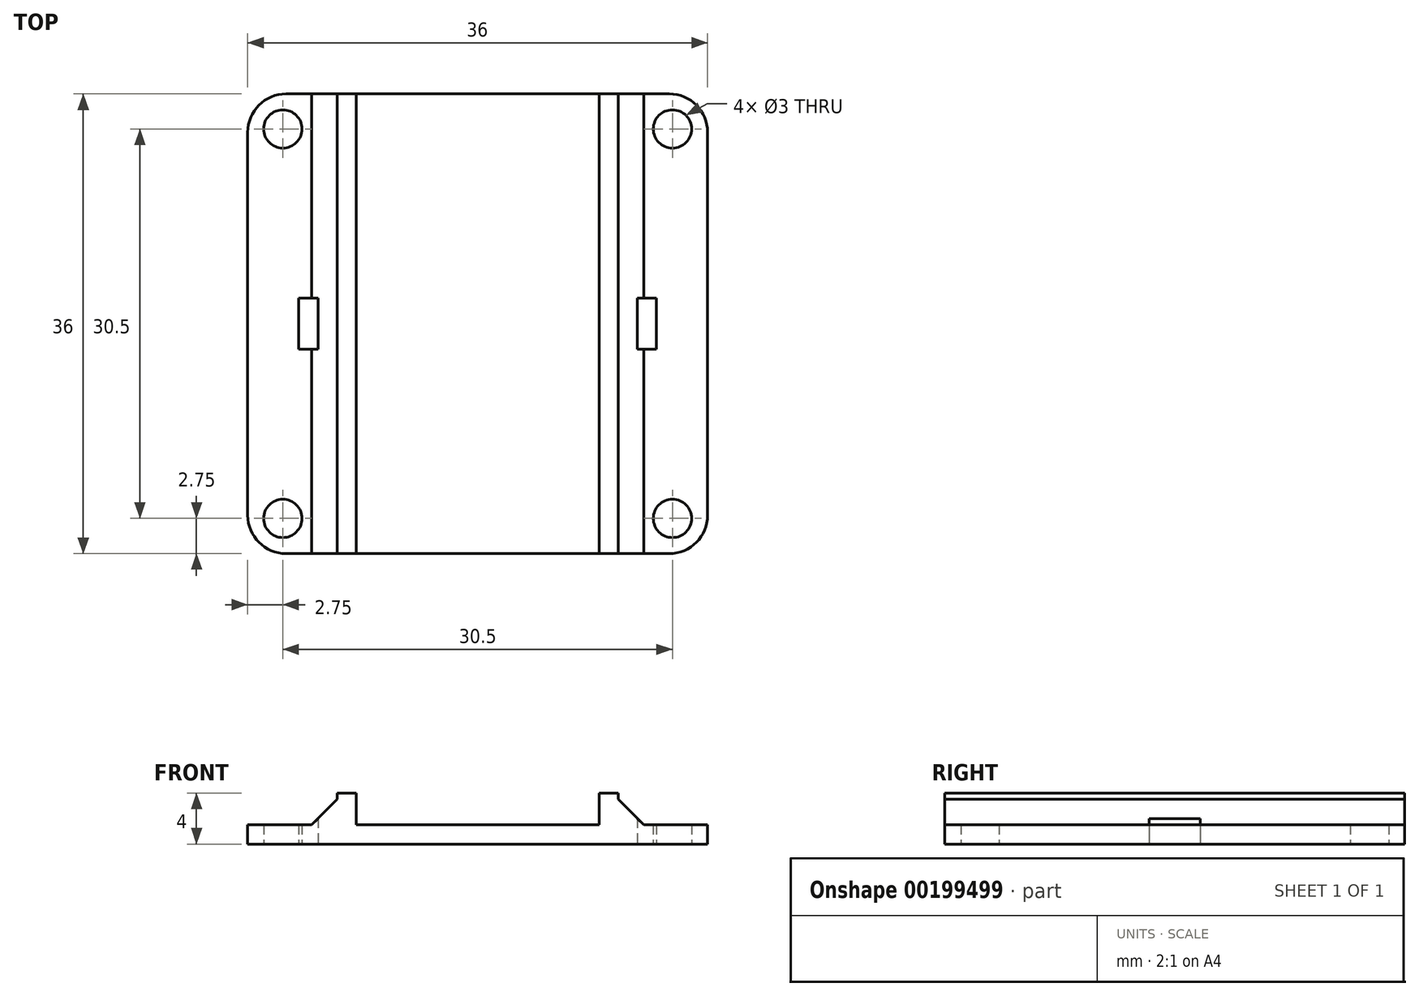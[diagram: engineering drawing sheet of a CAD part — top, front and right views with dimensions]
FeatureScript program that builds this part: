
annotation { "Feature Type Name" : "Feature", "Feature Type Description" : "" }
export const myFeature = defineFeature(function(context is Context, id is Id, definition is map)
    precondition{}
    {
        {
            var Q0;
            Q0=qCreatedBy(makeId("Top.planeOp"),FACE);
            var sketch = newSketch(context, id + "F0", { "sketchPlane" : qUnion([Q0])});
            skLineSegment(sketch, "E0.bottom", {"start": v(18, 18) * mm, "end": v(-18, 18) * mm});
            skLineSegment(sketch, "E0.top", {"start": v(18, -18) * mm, "end": v(-18, -18) * mm});
            skLineSegment(sketch, "E0.left", {"start": v(18, 18) * mm, "end": v(18, -18) * mm});
            skLineSegment(sketch, "E0.right", {"start": v(-18, 18) * mm, "end": v(-18, -18) * mm});
            skPoint(sketch, "E0.middle", {"position": v(0, 0) * mm});
            skLineSegment(sketch, "E1.bottom", {"start": v(15.25, 15.25) * mm, "end": v(-15.25, 15.25) * mm, "construction": true});
            skLineSegment(sketch, "E1.top", {"start": v(15.25, -15.25) * mm, "end": v(-15.25, -15.25) * mm, "construction": true});
            skLineSegment(sketch, "E1.left", {"start": v(15.25, 15.25) * mm, "end": v(15.25, -15.25) * mm, "construction": true});
            skLineSegment(sketch, "E1.right", {"start": v(-15.25, 15.25) * mm, "end": v(-15.25, -15.25) * mm, "construction": true});
            skCircle(sketch, "E2", {"center": v(-15.25, 15.25) * mm, "radius": 1.5 * mm});
            skCircle(sketch, "E3", {"center": v(15.25, 15.25) * mm, "radius": 1.5 * mm});
            skCircle(sketch, "E4", {"center": v(15.25, -15.25) * mm, "radius": 1.5 * mm});
            skCircle(sketch, "E5", {"center": v(-15.25, -15.25) * mm, "radius": 1.5 * mm});
            skLineSegment(sketch, "E6.bottom", {"start": v(-9.5, 18) * mm, "end": v(9.5, 18) * mm});
            skLineSegment(sketch, "E6.top", {"start": v(-9.5, -18) * mm, "end": v(9.5, -18) * mm});
            skLineSegment(sketch, "E6.left", {"start": v(-9.5, 18) * mm, "end": v(-9.5, -18) * mm});
            skLineSegment(sketch, "E6.right", {"start": v(9.5, 18) * mm, "end": v(9.5, -18) * mm});
            skLineSegment(sketch, "E7.bottom", {"start": v(-11, 18) * mm, "end": v(11, 18) * mm});
            skLineSegment(sketch, "E7.top", {"start": v(-11, -18) * mm, "end": v(11, -18) * mm});
            skLineSegment(sketch, "E7.left", {"start": v(-11, 18) * mm, "end": v(-11, -18) * mm});
            skLineSegment(sketch, "E7.right", {"start": v(11, 18) * mm, "end": v(11, -18) * mm});
            skPoint(sketch, "E8.centerSnap0", {"position": v(-15.25, 0) * mm});
            skPoint(sketch, "E9.centerSnap0", {"position": v(15.25, 0) * mm});
            skLineSegment(sketch, "E10", {"start": v(-11, 0) * mm, "end": v(-9.5, 0) * mm, "construction": true});
            skLineSegment(sketch, "E11", {"start": v(9.5, 0) * mm, "end": v(11, 0) * mm, "construction": true});
            skLineSegment(sketch, "E12.bottom", {"start": v(11, 2) * mm, "end": v(9.5, 2) * mm});
            skLineSegment(sketch, "E12.top", {"start": v(11, -2) * mm, "end": v(9.5, -2) * mm});
            skLineSegment(sketch, "E12.left", {"start": v(11, 2) * mm, "end": v(11, -2) * mm});
            skLineSegment(sketch, "E12.right", {"start": v(9.5, 2) * mm, "end": v(9.5, -2) * mm});
            skPoint(sketch, "E12.middle", {"position": v(10.25, 0) * mm});
            skLineSegment(sketch, "E13.bottom", {"start": v(-9.5, 2) * mm, "end": v(-11, 2) * mm});
            skLineSegment(sketch, "E13.top", {"start": v(-9.5, -2) * mm, "end": v(-11, -2) * mm});
            skLineSegment(sketch, "E13.left", {"start": v(-9.5, 2) * mm, "end": v(-9.5, -2) * mm});
            skLineSegment(sketch, "E13.right", {"start": v(-11, 2) * mm, "end": v(-11, -2) * mm});
            skPoint(sketch, "E13.middle", {"position": v(-10.25, 0) * mm});
            skLineSegment(sketch, "E14", {"start": v(-11, 2) * mm, "end": v(-12.5, 2) * mm, "construction": true});
            skLineSegment(sketch, "E15", {"start": v(-11, -2) * mm, "end": v(-12.5, -2) * mm, "construction": true});
            skLineSegment(sketch, "E16.bottom", {"start": v(-12.5, -2) * mm, "end": v(-14, -2) * mm});
            skLineSegment(sketch, "E16.top", {"start": v(-12.5, 2) * mm, "end": v(-14, 2) * mm});
            skLineSegment(sketch, "E16.left", {"start": v(-12.5, -2) * mm, "end": v(-12.5, 2) * mm});
            skLineSegment(sketch, "E16.right", {"start": v(-14, -2) * mm, "end": v(-14, 2) * mm});
            skLineSegment(sketch, "E17", {"start": v(0, -18) * mm, "end": v(0, 18) * mm, "construction": true});
            skLineSegment(sketch, "E18.MirrorCS", {"start": v(12.5, -2) * mm, "end": v(14, -2) * mm});
            skLineSegment(sketch, "E19.MirrorCS", {"start": v(14, -2) * mm, "end": v(14, 2) * mm});
            skLineSegment(sketch, "E20.MirrorCS", {"start": v(12.5, 2) * mm, "end": v(14, 2) * mm});
            skLineSegment(sketch, "E21.MirrorCS", {"start": v(12.5, -2) * mm, "end": v(12.5, 2) * mm});
            skSolve(sketch);
        }
        {
            var Q0;
            {var subQ0=sQuery(id+"F0.wireOp",EDGE,"E0.right");Q0=makeQuery(id+"F0.imprint","IMPRINT",FACE,{"disambiguationData":[TD([[makeQuery(id+"F0.imprint","IMPRINT",EDGE,{"derivedFrom":subQ0}),1.0]])]});}
            var Q1;
            {var subQ0=sQuery(id+"F0.wireOp",EDGE,"E6.left");Q1=makeQuery(id+"F0.imprint","IMPRINT",FACE,{"disambiguationData":[TD([[makeQuery(id+"F0.imprint","IMPRINT",EDGE,{"derivedFrom":subQ0}),-1.0]])]});}
            var Q2;
            {var subQ0=sQuery(id+"F0.wireOp",EDGE,"E6.right");Q2=makeQuery(id+"F0.imprint","IMPRINT",FACE,{"disambiguationData":[TD([[makeQuery(id+"F0.imprint","IMPRINT",EDGE,{"derivedFrom":subQ0}),1.0]])]});}
            var Q3;
            {var subQ0=sQuery(id+"F0.wireOp",EDGE,"E0.left");Q3=makeQuery(id+"F0.imprint","IMPRINT",FACE,{"disambiguationData":[TD([[makeQuery(id+"F0.imprint","IMPRINT",EDGE,{"derivedFrom":subQ0}),-1.0]])]});}
            var Q4;
            {var subQ0=sQuery(id+"F0.wireOp",EDGE,"E6.left");Q4=makeQuery(id+"F0.imprint","IMPRINT",FACE,{"disambiguationData":[TD([[makeQuery(id+"F0.imprint","IMPRINT",EDGE,{"derivedFrom":subQ0}),1.0]])]});}
            var Q5;
            Q5=makeQuery(id+"F0.imprint","IMPRINT",FACE,{"disambiguationData":[TD([[makeQuery(id+"F0.imprint","IMPRINT",EDGE,{"derivedFrom":sQuery(id+"F0.wireOp",EDGE,"E13.bottom")}),1.0]])]});
            var Q6;
            Q6=makeQuery(id+"F0.imprint","IMPRINT",FACE,{"disambiguationData":[TD([[makeQuery(id+"F0.imprint","IMPRINT",EDGE,{"derivedFrom":sQuery(id+"F0.wireOp",EDGE,"E12.bottom")}),1.0]])]});
            extrude(context, id + "F1", {"entities" : qUnion([Q0, Q1, Q2, Q3, Q4, Q5, Q6]), "depth" : 1.5 * mm});
        }
        {
            var Q0;
            {var subQ0=sQuery(id+"F0.wireOp",EDGE,"E6.left");Q0=makeQuery(id+"F0.imprint","IMPRINT",FACE,{"disambiguationData":[TD([[makeQuery(id+"F0.imprint","IMPRINT",EDGE,{"derivedFrom":subQ0}),-1.0]])]});}
            var Q1;
            {var subQ0=sQuery(id+"F0.wireOp",EDGE,"E6.right");Q1=makeQuery(id+"F0.imprint","IMPRINT",FACE,{"disambiguationData":[TD([[makeQuery(id+"F0.imprint","IMPRINT",EDGE,{"derivedFrom":subQ0}),1.0]])]});}
            extrude(context, id + "F2", {"entities" : qUnion([Q0, Q1]), "operationType" : NewBodyOperationType.ADD, "depth" : 4 * mm});
        }
        {
            var Q0;
            Q0=makeQuery(id+"F1.opExtrude","SWEPT_EDGE",EDGE,{"disambiguationData":[OSD([sQuery(id+"F0.wireOp",EDGE,"E0.top"),sQuery(id+"F0.wireOp",EDGE,"E0.right")])]});
            var Q1;
            Q1=makeQuery(id+"F1.opExtrude","SWEPT_EDGE",EDGE,{"disambiguationData":[OSD([sQuery(id+"F0.wireOp",EDGE,"E0.top"),sQuery(id+"F0.wireOp",EDGE,"E0.left")])]});
            var Q2;
            Q2=makeQuery(id+"F1.opExtrude","SWEPT_EDGE",EDGE,{"disambiguationData":[OSD([sQuery(id+"F0.wireOp",EDGE,"E0.bottom"),sQuery(id+"F0.wireOp",EDGE,"E0.left")])]});
            var Q3;
            Q3=makeQuery(id+"F1.opExtrude","SWEPT_EDGE",EDGE,{"disambiguationData":[OSD([sQuery(id+"F0.wireOp",EDGE,"E0.bottom"),sQuery(id+"F0.wireOp",EDGE,"E0.right")])]});
            fillet(context, id + "F3", {"entities" : qUnion([Q0, Q1, Q2, Q3]), "radius" : 3 * mm, "tangentPropagation" : true, "allowEdgeOverflow" : false});
        }
        {
            var Q0;
            {var subQ0=sQuery(id+"F0.wireOp",EDGE,"E7.left");var subQ1=sQuery(id+"F0.wireOp",EDGE,"E7.top");var subQ2=sQuery(id+"F0.wireOp",EDGE,"E0.top");Q0=makeQuery(id+"F2.boolean.opBoolean","INTERSECT",EDGE,{"derivedFrom":[makeQuery(id+"F1.opExtrude","CAP_FACE",FACE,{"disambiguationData":[OSD([sQuery(id+"F0.wireOp",EDGE,"E0.bottom"),subQ2,sQuery(id+"F0.wireOp",EDGE,"E0.left"),sQuery(id+"F0.wireOp",EDGE,"E0.right"),sQuery(id+"F0.wireOp",EDGE,"E2"),sQuery(id+"F0.wireOp",EDGE,"E3"),sQuery(id+"F0.wireOp",EDGE,"E4"),sQuery(id+"F0.wireOp",EDGE,"E5"),sQuery(id+"F0.wireOp",EDGE,"E7.bottom"),subQ1,sQuery(id+"F0.wireOp",EDGE,"E8"),sQuery(id+"F0.wireOp",EDGE,"E9")])],"isStart":false}),makeQuery(id+"F2.opExtrude","SWEPT_FACE",FACE,{"disambiguationData":[OSD([subQ0]),TDD([makeQuery(id+"F0.imprint","IMPRINT",EDGE,{"disambiguationData":[TD([[makeQuery(id+"F0.imprint","INTERSECT",VERTEX,{"derivedFrom":[subQ2,subQ1,subQ0]}),1.0]])],"derivedFrom":subQ0})])]})]});}
            var Q1;
            {var subQ0=sQuery(id+"F0.wireOp",EDGE,"E7.left");var subQ1=sQuery(id+"F0.wireOp",EDGE,"E7.bottom");var subQ2=sQuery(id+"F0.wireOp",EDGE,"E0.bottom");Q1=makeQuery(id+"F2.boolean.opBoolean","INTERSECT",EDGE,{"derivedFrom":[makeQuery(id+"F1.opExtrude","CAP_FACE",FACE,{"disambiguationData":[OSD([subQ2,sQuery(id+"F0.wireOp",EDGE,"E0.top"),sQuery(id+"F0.wireOp",EDGE,"E0.left"),sQuery(id+"F0.wireOp",EDGE,"E0.right"),sQuery(id+"F0.wireOp",EDGE,"E2"),sQuery(id+"F0.wireOp",EDGE,"E3"),sQuery(id+"F0.wireOp",EDGE,"E4"),sQuery(id+"F0.wireOp",EDGE,"E5"),subQ1,sQuery(id+"F0.wireOp",EDGE,"E7.top"),sQuery(id+"F0.wireOp",EDGE,"E8"),sQuery(id+"F0.wireOp",EDGE,"E9")])],"isStart":false}),makeQuery(id+"F2.opExtrude","SWEPT_FACE",FACE,{"disambiguationData":[OSD([subQ0]),TDD([makeQuery(id+"F0.imprint","IMPRINT",EDGE,{"disambiguationData":[TD([[makeQuery(id+"F0.imprint","INTERSECT",VERTEX,{"derivedFrom":[subQ2,subQ1,subQ0]}),-1.0]])],"derivedFrom":subQ0})])]})]});}
            var Q2;
            {var subQ0=sQuery(id+"F0.wireOp",EDGE,"E7.right");var subQ1=sQuery(id+"F0.wireOp",EDGE,"E7.top");var subQ2=sQuery(id+"F0.wireOp",EDGE,"E0.top");Q2=makeQuery(id+"F2.boolean.opBoolean","INTERSECT",EDGE,{"derivedFrom":[makeQuery(id+"F1.opExtrude","CAP_FACE",FACE,{"disambiguationData":[OSD([sQuery(id+"F0.wireOp",EDGE,"E0.bottom"),subQ2,sQuery(id+"F0.wireOp",EDGE,"E0.left"),sQuery(id+"F0.wireOp",EDGE,"E0.right"),sQuery(id+"F0.wireOp",EDGE,"E2"),sQuery(id+"F0.wireOp",EDGE,"E3"),sQuery(id+"F0.wireOp",EDGE,"E4"),sQuery(id+"F0.wireOp",EDGE,"E5"),sQuery(id+"F0.wireOp",EDGE,"E7.bottom"),subQ1,sQuery(id+"F0.wireOp",EDGE,"E8"),sQuery(id+"F0.wireOp",EDGE,"E9")])],"isStart":false}),makeQuery(id+"F2.opExtrude","SWEPT_FACE",FACE,{"disambiguationData":[OSD([subQ0]),TDD([makeQuery(id+"F0.imprint","IMPRINT",EDGE,{"disambiguationData":[TD([[makeQuery(id+"F0.imprint","INTERSECT",VERTEX,{"derivedFrom":[subQ2,subQ1,subQ0]}),1.0]])],"derivedFrom":subQ0})])]})]});}
            var Q3;
            {var subQ0=sQuery(id+"F0.wireOp",EDGE,"E7.right");var subQ1=sQuery(id+"F0.wireOp",EDGE,"E7.bottom");var subQ2=sQuery(id+"F0.wireOp",EDGE,"E0.bottom");Q3=makeQuery(id+"F2.boolean.opBoolean","INTERSECT",EDGE,{"derivedFrom":[makeQuery(id+"F1.opExtrude","CAP_FACE",FACE,{"disambiguationData":[OSD([subQ2,sQuery(id+"F0.wireOp",EDGE,"E0.top"),sQuery(id+"F0.wireOp",EDGE,"E0.left"),sQuery(id+"F0.wireOp",EDGE,"E0.right"),sQuery(id+"F0.wireOp",EDGE,"E2"),sQuery(id+"F0.wireOp",EDGE,"E3"),sQuery(id+"F0.wireOp",EDGE,"E4"),sQuery(id+"F0.wireOp",EDGE,"E5"),subQ1,sQuery(id+"F0.wireOp",EDGE,"E7.top"),sQuery(id+"F0.wireOp",EDGE,"E8"),sQuery(id+"F0.wireOp",EDGE,"E9")])],"isStart":false}),makeQuery(id+"F2.opExtrude","SWEPT_FACE",FACE,{"disambiguationData":[OSD([subQ0]),TDD([makeQuery(id+"F0.imprint","IMPRINT",EDGE,{"disambiguationData":[TD([[makeQuery(id+"F0.imprint","INTERSECT",VERTEX,{"derivedFrom":[subQ2,subQ1,subQ0]}),-1.0]])],"derivedFrom":subQ0})])]})]});}
            chamfer(context, id + "F4", {"entities" : qUnion([Q0, Q1, Q2, Q3]), "width" : 2 * mm, "tangentPropagation" : true});
        }
    });
